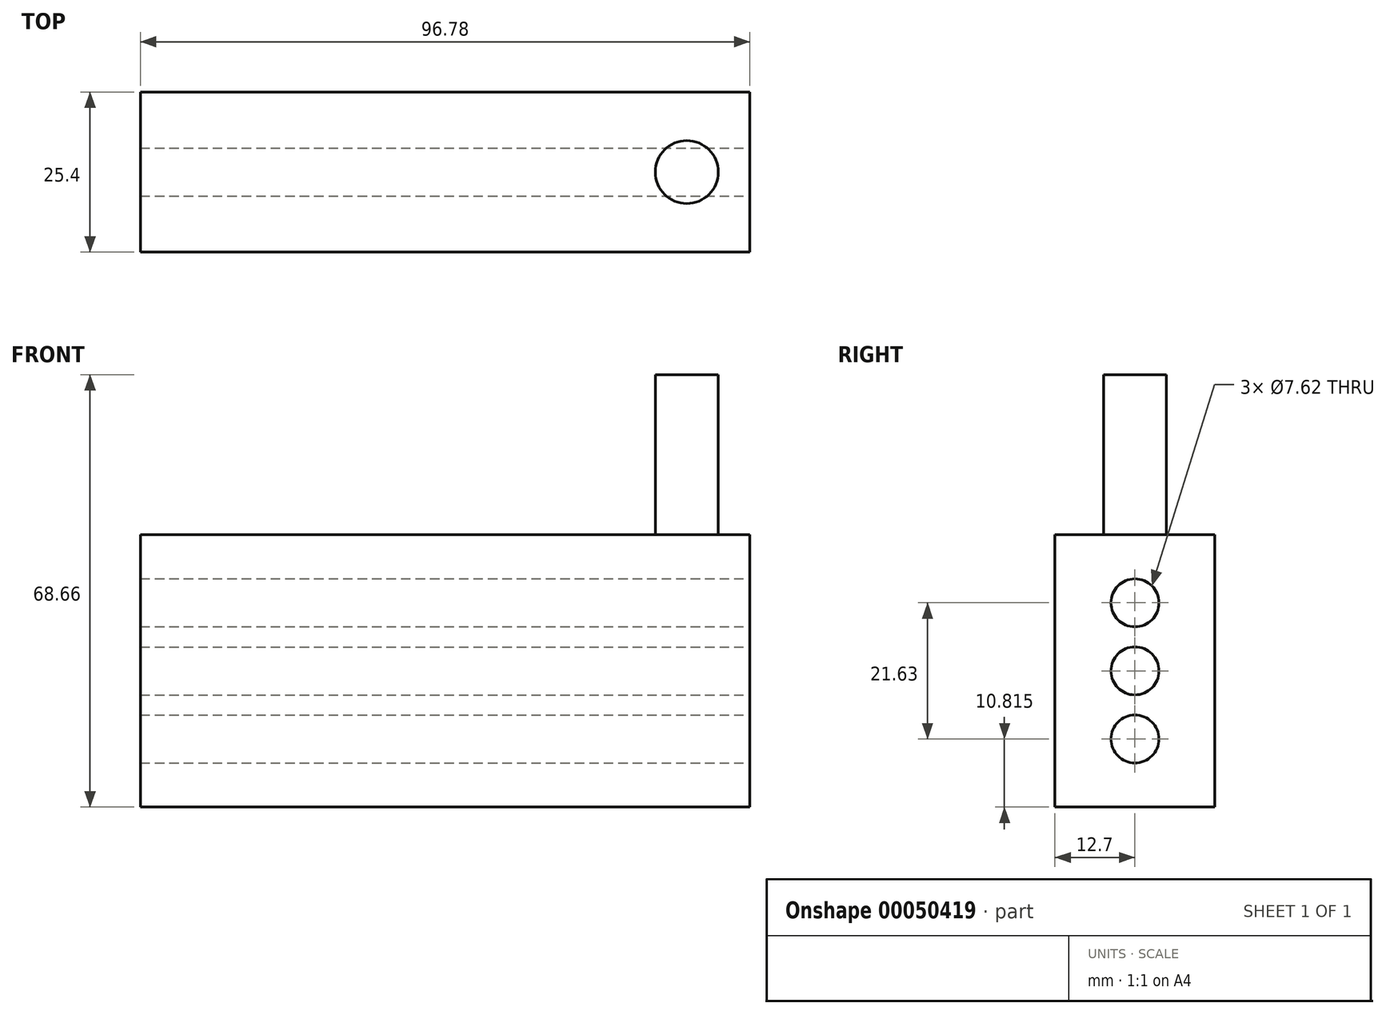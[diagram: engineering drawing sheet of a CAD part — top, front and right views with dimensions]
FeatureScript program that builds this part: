
annotation { "Feature Type Name" : "Feature", "Feature Type Description" : "" }
export const myFeature = defineFeature(function(context is Context, id is Id, definition is map)
    precondition{}
    {
        {
            var Q0;
            Q0=qCreatedBy(makeId("Front.planeOp"),FACE);
            var sketch = newSketch(context, id + "F0", { "sketchPlane" : qUnion([Q0])});
            skLineSegment(sketch, "E0.rect.bottom", {"start": v(48.4, -21.63) * mm, "end": v(-48.4, -21.63) * mm});
            skLineSegment(sketch, "E0.rect.top", {"start": v(48.4, 21.63) * mm, "end": v(-48.4, 21.63) * mm});
            skLineSegment(sketch, "E0.rect.left", {"start": v(48.4, -21.63) * mm, "end": v(48.4, 21.63) * mm});
            skLineSegment(sketch, "E0.rect.right", {"start": v(-48.4, -21.63) * mm, "end": v(-48.4, 21.63) * mm});
            skPoint(sketch, "E0.rect.middle", {"position": v(0, 0) * mm});
            skSolve(sketch);
        }
        {
            var Q0;
            Q0=makeQuery(id+"F0.imprint","IMPRINT",FACE,{"disambiguationData":[TD([[makeQuery(id+"F0.imprint","IMPRINT",EDGE,{"derivedFrom":sQuery(id+"F0.wireOp",EDGE,"E0.rect.bottom")}),-1.0]])]});
            extrude(context, id + "F6", {"entities" : qUnion([Q0]), "depth" : 25.4 * mm});
        }
        {
            var Q0;
            Q0=makeQuery(id+"F6.opExtrude","SWEPT_FACE",FACE,{"disambiguationData":[OSD([sQuery(id+"F0.wireOp",EDGE,"E0.rect.top")])]});
            var sketch = newSketch(context, id + "F1", { "sketchPlane" : qUnion([Q0])});
            skCircle(sketch, "E1", {"center": v(38.4, -12.7) * mm, "radius": 5 * mm});
            skSolve(sketch);
        }
        {
            var Q0;
            Q0 = qSketchRegion(id + "F1", true);
            extrude(context, id + "F2", {"entities" : qUnion([Q0]), "operationType" : NewBodyOperationType.ADD, "depth" : 25.4 * mm});
        }
        {
            var Q0;
            Q0=makeQuery(id+"F6.opExtrude","SWEPT_FACE",FACE,{"disambiguationData":[OSD([sQuery(id+"F0.wireOp",EDGE,"E0.rect.left")])]});
            var sketch = newSketch(context, id + "F3", { "sketchPlane" : qUnion([Q0])});
            skSolve(sketch);
        }
        {
            var Q0;
            {var subQ0=sQuery(id+"F0.wireOp",EDGE,"E0.rect.left");Q0=makeQuery(id+"F3.imprint","IMPRINT",FACE,{"disambiguationData":[TD([[makeQuery(id+"F3.imprint","IMPRINT",EDGE,{"derivedFrom":makeQuery(id+"F6.opExtrude","CAP_EDGE",EDGE,{"disambiguationData":[OSD([subQ0])],"isStart":true})}),1.0]])]});}
            var sketch = newSketch(context, id + "F7", { "sketchPlane" : qUnion([Q0])});
            skCircle(sketch, "E2", {"center": v(-12.7, 10.82) * mm, "radius": 3.81 * mm});
            skCircle(sketch, "E3", {"center": v(-12.7, 0) * mm, "radius": 3.81 * mm});
            skCircle(sketch, "E4", {"center": v(-12.7, -10.82) * mm, "radius": 3.81 * mm});
            skLineSegment(sketch, "E5", {"start": v(-12.7, 21.63) * mm, "end": v(-12.7, 10.82) * mm, "construction": true});
            skLineSegment(sketch, "E6", {"start": v(-12.7, 10.82) * mm, "end": v(-12.7, 0) * mm, "construction": true});
            skLineSegment(sketch, "E7", {"start": v(-12.7, 0) * mm, "end": v(-12.7, -10.82) * mm, "construction": true});
            skSolve(sketch);
        }
        {
            var Q0;
            Q0 = qSketchRegion(id + "F7", true);
            extrude(context, id + "F8", {"entities" : qUnion([Q0]), "operationType" : NewBodyOperationType.REMOVE, "endBound" : BoundingType.THROUGH_ALL, "oppositeDirection" : true, "depth" : 25.4 * mm});
        }
    });
